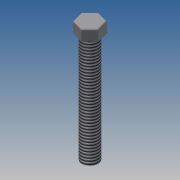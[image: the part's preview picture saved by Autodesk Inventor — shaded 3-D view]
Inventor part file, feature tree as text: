
AUTODESK INVENTOR PART (.ipt)
format: ipt  version: 2014 SP1 (Build 180222100, 222)  size: 95,232 bytes
history: native  units: in
note: dims shown in document units (in); Inventor stores cm internally (conversion verified against a paired STEP export)
features: extrude x2, sketch x2, fillet x1, thread x1
ambient origin geometry x8: Origin, YZ Plane, XZ Plane, XY Plane, X Axis, Y Axis, Z Axis, Center Point
bodies: Solid1 (feature_tree)
feature tree (6):
  extrude  "Extrusion1"  Depth=0.03in
  fillet  "Fillet1"  Radius=0.366in
  extrude  "Extrusion2"  Depth=2.5in TaperAngle=0.0deg
  thread  "Thread1"  [1 undecoded]
  sketch  "Sketch1"  dims[d0=0.25in d1=0.0in d2=0.03in d3=0.366in]
  sketch  "Sketch2"  dims[d4=2.5in d5=0.0in d6=1.0in d7=0.0in]
note: 1 required parameter value undecoded (feature->parameter linkage not recoverable at this tier; creation-order binding heuristic only, values carry confidence <= 0.55)
